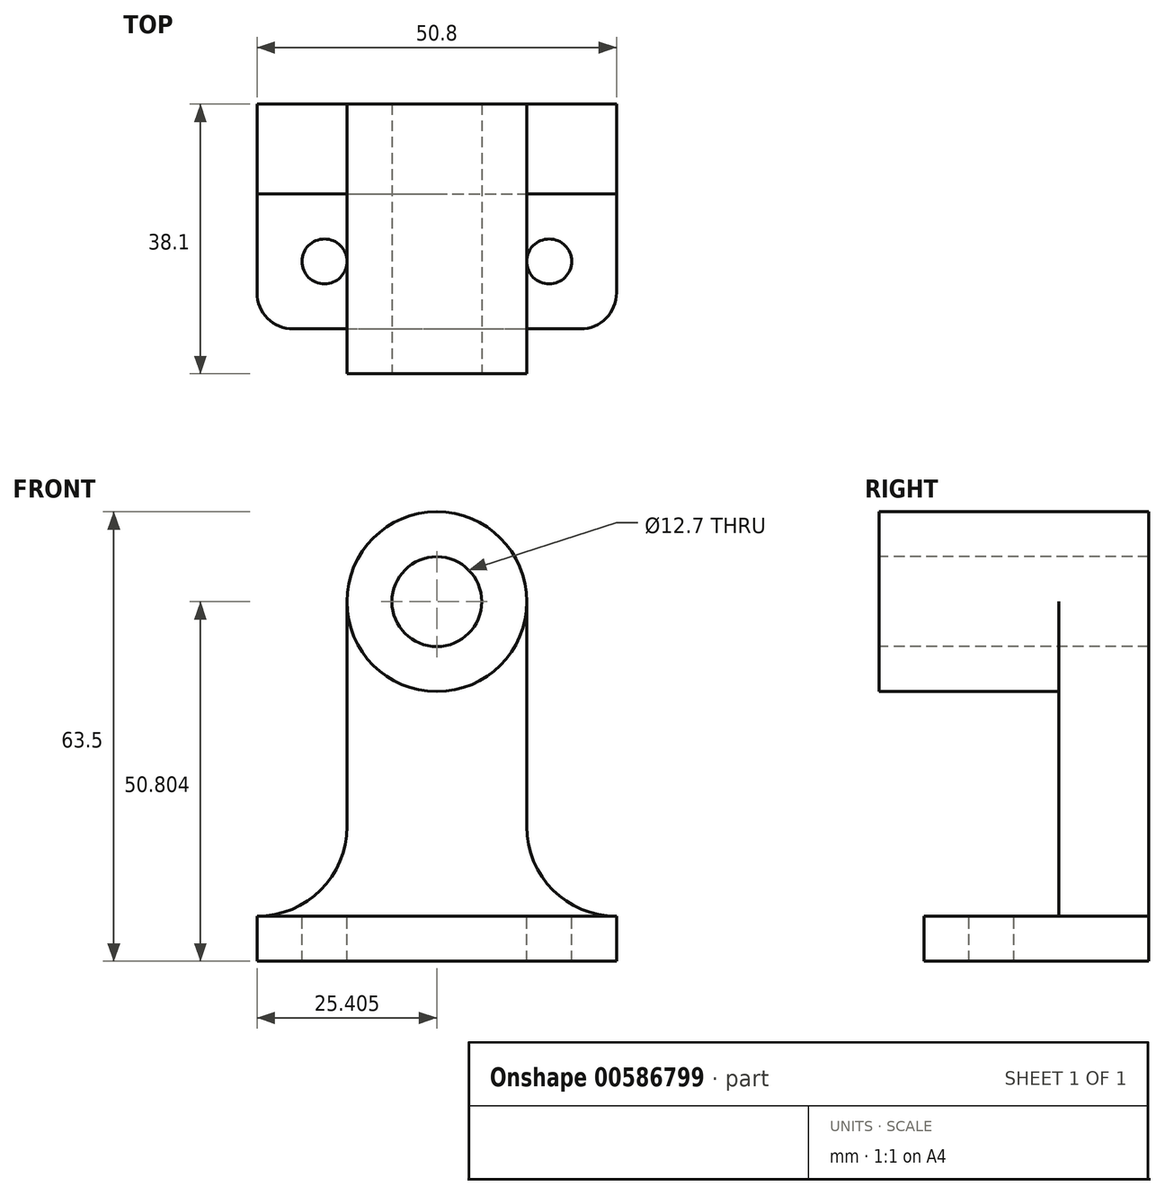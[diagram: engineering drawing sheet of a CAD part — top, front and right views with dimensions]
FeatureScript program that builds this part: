
annotation { "Feature Type Name" : "Feature", "Feature Type Description" : "" }
export const myFeature = defineFeature(function(context is Context, id is Id, definition is map)
    precondition{}
    {
        {
            var Q0;
            Q0=qCreatedBy(makeId("Front.planeOp"),FACE);
            var sketch = newSketch(context, id + "F0", { "sketchPlane" : qUnion([Q0])});
            skLineSegment(sketch, "E0", {"start": v(-66.3, 16.9) * mm, "end": v(-66.3, 6.23) * mm});
            skLineSegment(sketch, "E1", {"start": v(-66.3, 6.23) * mm, "end": v(-15.5, 6.23) * mm});
            skLineSegment(sketch, "E2", {"start": v(-15.5, 6.23) * mm, "end": v(-15.5, 16.9) * mm});
            skLineSegment(sketch, "E3", {"start": v(-15.5, 16.9) * mm, "end": v(-66.3, 16.9) * mm});
            skLineSegment(sketch, "E4", {"start": v(-66.3, 16.9) * mm, "end": v(-66.3, 69.73) * mm});
            skLineSegment(sketch, "E5", {"start": v(-66.3, 69.73) * mm, "end": v(-15.5, 69.73) * mm});
            skLineSegment(sketch, "E6", {"start": v(-15.5, 69.73) * mm, "end": v(-15.5, 16.9) * mm});
            skSolve(sketch);
        }
        {
            var Q0;
            Q0=makeQuery(id+"F0.imprint","IMPRINT",FACE,{"disambiguationData":[TD([[makeQuery(id+"F0.imprint","IMPRINT",EDGE,{"derivedFrom":sQuery(id+"F0.wireOp",EDGE,"E3")}),-1.0]])]});
            var Q1;
            Q1=makeQuery(id+"F0.imprint","IMPRINT",FACE,{"disambiguationData":[TD([[makeQuery(id+"F0.imprint","IMPRINT",EDGE,{"derivedFrom":sQuery(id+"F0.wireOp",EDGE,"E0")}),1.0]])]});
            extrude(context, id + "F1", {"entities" : qUnion([Q0, Q1]), "depth" : 12.7 * mm, "offsetDistance" : 25.4 * mm});
        }
        {
            var Q0;
            Q0=makeQuery(id+"F1.opExtrude","CAP_FACE",FACE,{"disambiguationData":[OSD([sQuery(id+"F0.wireOp",EDGE,"E0"),sQuery(id+"F0.wireOp",EDGE,"E1"),sQuery(id+"F0.wireOp",EDGE,"E2"),sQuery(id+"F0.wireOp",EDGE,"E4"),sQuery(id+"F0.wireOp",EDGE,"E5"),sQuery(id+"F0.wireOp",EDGE,"E6")])],"isStart":false});
            var sketch = newSketch(context, id + "F2", { "sketchPlane" : qUnion([Q0])});
            skLineSegment(sketch, "E7", {"start": v(-66.3, 12.58) * mm, "end": v(-15.5, 12.58) * mm});
            skSolve(sketch);
        }
        {
            var Q0;
            {var subQ0=sQuery(id+"F2.wireOp",EDGE,"E7");Q0=makeQuery(id+"F2.imprint","IMPRINT",FACE,{"disambiguationData":[TD([[makeQuery(id+"F2.imprint","IMPRINT",EDGE,{"derivedFrom":subQ0}),-1.0]])]});}
            extrude(context, id + "F3", {"entities" : qUnion([Q0]), "operationType" : NewBodyOperationType.ADD, "depth" : 19.05 * mm, "offsetDistance" : 25.4 * mm});
        }
        {
            var Q0;
            Q0=makeQuery(id+"F1.opExtrude","CAP_FACE",FACE,{"disambiguationData":[OSD([sQuery(id+"F0.wireOp",EDGE,"E0"),sQuery(id+"F0.wireOp",EDGE,"E1"),sQuery(id+"F0.wireOp",EDGE,"E2"),sQuery(id+"F0.wireOp",EDGE,"E4"),sQuery(id+"F0.wireOp",EDGE,"E5"),sQuery(id+"F0.wireOp",EDGE,"E6")])],"isStart":false});
            var sketch = newSketch(context, id + "F4", { "sketchPlane" : qUnion([Q0])});
            skCircle(sketch, "E8", {"center": v(-40.9, 57.03) * mm, "radius": 12.7 * mm});
            skLineSegment(sketch, "E9", {"start": v(-53.6, 57.03) * mm, "end": v(-53.6, 12.58) * mm});
            skLineSegment(sketch, "E10", {"start": v(-28.2, 57.03) * mm, "end": v(-28.2, 12.58) * mm});
            skArc(sketch, "E11", {"start": v(-66.3, 12.58) * mm, "mid": v(-57.32, 16.3) * mm, "end": v(-53.6, 25.28) * mm});
            skArc(sketch, "E12", {"start": v(-28.2, 25.28) * mm, "mid": v(-24.49, 16.3) * mm, "end": v(-15.5, 12.58) * mm});
            skSolve(sketch);
        }
        {
            var Q0;
            {var subQ1=sQuery(id+"F4.wireOp",EDGE,"E11");Q0=makeQuery(id+"F4.imprint","IMPRINT",FACE,{"disambiguationData":[TD([[makeQuery(id+"F4.imprint","IMPRINT",EDGE,{"derivedFrom":subQ1}),1.0]])]});}
            var Q1;
            {var subQ0=sQuery(id+"F4.wireOp",EDGE,"E12");Q1=makeQuery(id+"F4.imprint","IMPRINT",FACE,{"disambiguationData":[TD([[makeQuery(id+"F4.imprint","IMPRINT",EDGE,{"derivedFrom":subQ0}),1.0]])]});}
            extrude(context, id + "F5", {"entities" : qUnion([Q0, Q1]), "operationType" : NewBodyOperationType.REMOVE, "oppositeDirection" : true, "depth" : 25.4 * mm, "offsetDistance" : 25.4 * mm});
        }
        {
            var Q0;
            Q0=makeQuery(id+"F1.opExtrude","CAP_FACE",FACE,{"disambiguationData":[OSD([sQuery(id+"F0.wireOp",EDGE,"E0"),sQuery(id+"F0.wireOp",EDGE,"E1"),sQuery(id+"F0.wireOp",EDGE,"E2"),sQuery(id+"F0.wireOp",EDGE,"E4"),sQuery(id+"F0.wireOp",EDGE,"E5"),sQuery(id+"F0.wireOp",EDGE,"E6")])],"isStart":false});
            var sketch = newSketch(context, id + "F6", { "sketchPlane" : qUnion([Q0])});
            skCircle(sketch, "E13", {"center": v(-40.9, 57.03) * mm, "radius": 12.7 * mm});
            skSolve(sketch);
        }
        {
            var Q0;
            {var subQ0=sQuery(id+"F6.wireOp",EDGE,"E13");var subQ1=makeQuery(id+"F6.imprint","INTERSECT",VERTEX,{"derivedFrom":[makeQuery(id+"F5.boolean.opBoolean","COPY",EDGE,{"derivedFrom":makeQuery(id+"F5.opExtrude","CAP_EDGE",EDGE,{"disambiguationData":[OSD([sQuery(id+"F4.wireOp",EDGE,"E9")])],"isStart":true})}),subQ0]});Q0=makeQuery(id+"F6.imprint","IMPRINT",FACE,{"disambiguationData":[TD([[makeQuery(id+"F6.imprint","IMPRINT",EDGE,{"disambiguationData":[TD([[subQ1,1.0]])],"derivedFrom":subQ0}),1.0]])]});}
            extrude(context, id + "F7", {"entities" : qUnion([Q0]), "operationType" : NewBodyOperationType.ADD, "depth" : 25.4 * mm, "offsetDistance" : 25.4 * mm});
        }
        {
            var Q0;
            Q0=makeQuery(id+"F7.opExtrude","CAP_FACE",FACE,{"disambiguationData":[OSD([sQuery(id+"F6.wireOp",EDGE,"E13")])],"isStart":false});
            var sketch = newSketch(context, id + "F8", { "sketchPlane" : qUnion([Q0])});
            skCircle(sketch, "E14", {"center": v(-40.9, 57.03) * mm, "radius": 6.35 * mm});
            skSolve(sketch);
        }
        {
            var Q0;
            Q0=sQuery(id+"F8.wireOp",VERTEX,"E14.center");
            var Q1;
            Q1=makeQuery(id+"F1.opExtrude","SWEPT_BODY",BODY,{"disambiguationData":[OSD([sQuery(id+"F0.wireOp",EDGE,"E0"),sQuery(id+"F0.wireOp",EDGE,"E1"),sQuery(id+"F0.wireOp",EDGE,"E2"),sQuery(id+"F0.wireOp",EDGE,"E4"),sQuery(id+"F0.wireOp",EDGE,"E5"),sQuery(id+"F0.wireOp",EDGE,"E6")])]});
            hole(context, id + "F9", {"style" : HoleStyle.SIMPLE, "endStyle" : HoleEndStyle.THROUGH, "holeDiameter" : 12.7 * mm, "majorDiameter" : 6.35 * mm, "isTappedThrough" : true, "tappedDepth" : 12.7 * mm, "tapClearance" : 3, "locations" : qUnion([Q0]), "scope" : qUnion([Q1])});
        }
        {
            var Q0;
            Q0=makeQuery(id+"F3.opExtrude","CAP_EDGE",EDGE,{"disambiguationData":[OSD([sQuery(id+"F0.wireOp",EDGE,"E0"),sQuery(id+"F0.wireOp",EDGE,"E4")])],"isStart":false});
            var Q1;
            Q1=makeQuery(id+"F3.opExtrude","CAP_EDGE",EDGE,{"disambiguationData":[OSD([sQuery(id+"F0.wireOp",EDGE,"E2"),sQuery(id+"F0.wireOp",EDGE,"E6")])],"isStart":false});
            fillet(context, id + "F10", {"entities" : qUnion([Q0, Q1]), "radius" : 5.08 * mm, "tangentPropagation" : true, "allowEdgeOverflow" : false});
        }
        {
            var Q0;
            Q0=makeQuery(id+"F3.opExtrude","SWEPT_FACE",FACE,{"disambiguationData":[OSD([sQuery(id+"F2.wireOp",EDGE,"E7")])]});
            var sketch = newSketch(context, id + "F11", { "sketchPlane" : qUnion([Q0])});
            skCircle(sketch, "E15", {"center": v(-56.78, -22.23) * mm, "radius": 3.17 * mm});
            skCircle(sketch, "E16", {"center": v(-25.03, -22.23) * mm, "radius": 3.18 * mm});
            skSolve(sketch);
        }
        {
            var Q0;
            Q0=sQuery(id+"F11.wireOp",VERTEX,"E15.center");
            var Q1;
            Q1=sQuery(id+"F11.wireOp",VERTEX,"E16.center");
            var Q2;
            Q2=makeQuery(id+"F1.opExtrude","SWEPT_BODY",BODY,{"disambiguationData":[OSD([sQuery(id+"F0.wireOp",EDGE,"E0"),sQuery(id+"F0.wireOp",EDGE,"E1"),sQuery(id+"F0.wireOp",EDGE,"E2"),sQuery(id+"F0.wireOp",EDGE,"E4"),sQuery(id+"F0.wireOp",EDGE,"E5"),sQuery(id+"F0.wireOp",EDGE,"E6")])]});
            hole(context, id + "F12", {"style" : HoleStyle.SIMPLE, "endStyle" : HoleEndStyle.THROUGH, "holeDiameter" : 6.35 * mm, "majorDiameter" : 6.35 * mm, "isTappedThrough" : true, "tappedDepth" : 12.7 * mm, "tapClearance" : 3, "locations" : qUnion([Q0, Q1]), "scope" : qUnion([Q2])});
        }
    });
